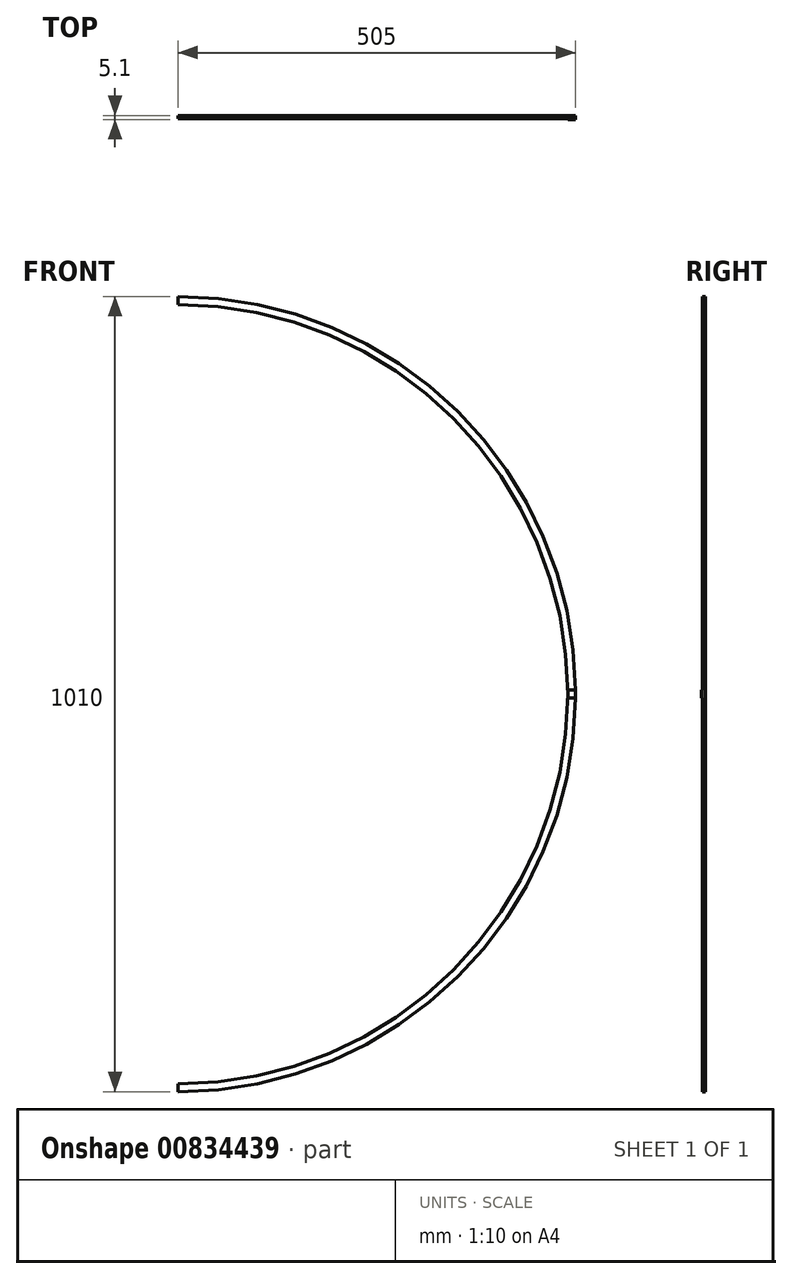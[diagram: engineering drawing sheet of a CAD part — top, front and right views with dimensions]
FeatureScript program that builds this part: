
annotation { "Feature Type Name" : "Feature", "Feature Type Description" : "" }
export const myFeature = defineFeature(function(context is Context, id is Id, definition is map)
    precondition{}
    {
        {
            var Q0;
            Q0=qCreatedBy(makeId("Front.planeOp"),FACE);
            var sketch = newSketch(context, id + "F0", { "sketchPlane" : qUnion([Q0])});
            skArc(sketch, "E0", {"start": v(0, -495) * mm, "mid": v(495, 0) * mm, "end": v(0, 495) * mm});
            skArc(sketch, "E1", {"start": v(0, -505) * mm, "mid": v(505, 0) * mm, "end": v(0, 505) * mm});
            skLineSegment(sketch, "E2", {"start": v(0, 505) * mm, "end": v(0, 495) * mm});
            skLineSegment(sketch, "E3.trimOffspring", {"start": v(0, -495) * mm, "end": v(0, -505) * mm});
            skPoint(sketch, "E4.orphan", {"position": v(0, 597.07) * mm});
            skSolve(sketch);
        }
        {
            var Q0;
            Q0 = qSketchRegion(id + "F0", true);
            extrude(context, id + "F1", {"entities" : qUnion([Q0]), "depth" : 4.1 * mm, "offsetDistance" : 25 * mm});
        }
        {
            var Q0;
            Q0=makeQuery(id+"F1.opExtrude","CAP_FACE",FACE,{"disambiguationData":[OSD([sQuery(id+"F0.wireOp",EDGE,"E0"),sQuery(id+"F0.wireOp",EDGE,"E1"),sQuery(id+"F0.wireOp",EDGE,"E2"),sQuery(id+"F0.wireOp",EDGE,"E3.trimOffspring")])],"isStart":false});
            var sketch = newSketch(context, id + "F2", { "sketchPlane" : qUnion([Q0])});
            skLineSegment(sketch, "E5", {"start": v(0, 0) * mm, "end": v(495, 0) * mm});
            skPoint(sketch, "E6", {"position": v(495, 0) * mm});
            skPoint(sketch, "E7", {"position": v(500, 0) * mm});
            skLineSegment(sketch, "E8.bottom", {"start": v(495, 5) * mm, "end": v(505, 5) * mm});
            skLineSegment(sketch, "E8.top", {"start": v(495, -5) * mm, "end": v(505, -5) * mm});
            skLineSegment(sketch, "E8.left", {"start": v(495, 5) * mm, "end": v(495, -5) * mm});
            skLineSegment(sketch, "E8.right", {"start": v(505, 5) * mm, "end": v(505, -5) * mm});
            skSolve(sketch);
        }
        {
            var Q0;
            {var subQ0=sQuery(id+"F2.wireOp",EDGE,"E8.left");var subQ2=sQuery(id+"F2.wireOp",EDGE,"E8.bottom");var subQ3=makeQuery(id+"F2.imprint","INTERSECT",VERTEX,{"derivedFrom":[subQ2,subQ0]});Q0=makeQuery(id+"F2.imprint","IMPRINT",FACE,{"disambiguationData":[TD([[makeQuery(id+"F2.imprint","IMPRINT",EDGE,{"disambiguationData":[TD([[subQ3,-1.0]])],"derivedFrom":subQ2}),-1.0]])]});}
            extrude(context, id + "F3", {"entities" : qUnion([Q0]), "operationType" : NewBodyOperationType.ADD, "depth" : 1 * mm, "offsetDistance" : 25 * mm});
        }
    });
